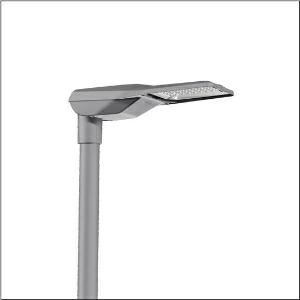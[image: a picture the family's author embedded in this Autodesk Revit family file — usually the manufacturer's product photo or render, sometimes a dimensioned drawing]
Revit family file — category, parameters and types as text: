
# Revit family: streetlight_sl_21_iq_mini___stw1_0a_5xe2e41g08jb_4c9f
name_source: partatom
category: Lighting Fixtures
units: mm (PartAtom-declared; Revit-internal decimal feet)

## family parameters
Cut with Voids When Loaded = No
Host = Face
Light Source = No
Part Type = Normal
Room Calculation Point = No
Round Connector Dimension = Use Diameter
Shared = No

## types (1)
- --- (1 x LED, 11290 lm, 71.6 W, 4000K)
    Apparent Load = 72 VA
    CIE Flux Codes = 39 75 98 100 100
    Color Rendering = 70
    Color Temperature = 4000K
    Default Elevation = 1800 mm
    Description = Streetlight SL 21 iQ mini, mast luminaire, primary light control with lens, of PMMA, primary optical cover: cover, of toughened safety glass, transparent, light distribution: STW1.0a, light emission: direct distribution, primary light characteristic: asymmetric, installation type: post-top, side-entry, LED, High Power LED, rated luminous flux: 11.290lm, luminous efficacy: 158lm/W, light colour: 740, colour temperature: 4000K, control: Street-Remote, Auto-Match, Temp-Guard, Lumen-Switch, Night-Set, Smart-Wire, Light-Fading, Desk-Remote (wireless, voltage-free reading and setting of iQ features in the workshop via application-optimized NFC function/RFID function), optimised constant luminous flux control (CLO 2.0), presetting dimming linear, mains connection: 220..240V, AC, 50/60Hz, start of lifetime: 72W, end of service life: 75W, reduction: 33W, luminaire housing, of diecast aluminium, powder-coated, Siteco® metallic grey (DB 702S), corrosivity category C5 mid according to DIN EN ISO 12944, please order mast flange separately, inclination adjustable: 0°, 5°, 10°, 15°, sealing non-destructively replaceable, multi-level sealing system, length: 628mm, width: 235mm, height: 110mm, mast flange for spigot size: 42mm (side-entry): 5XC10008XM4, 60/48mm (side-entry/post-top): 5XC10108XM2, 76/60mm (side-entry/post-top): 5XC10108XM1, protection rating (complete): IP66, insulation class (complete): insulation class II (safety insulation), certification: CE, ENEC, ENEC+, VDE, impact resistance: IK09, permissible operating ambient temperature for outdoor applications: -40..+50°C, standard-compliant lighting for roads and squares, packaging unit: 1 piece

Light Distribution: STW1.0a
    Height = 110 mm
    Lamp = 1 x LED
    Lamp Light Flux = 11290 lm
    Lamp Power = 71.6 W
    Lamp count = 1
    Length = 625 mm
    Luminous efficacy = 158 lm/W
    Manufacturer = Siteco
    ModVariant = No
    Model = 5XE2E41G08JB
    Number of Poles = 1
    OnlyDefault = Yes
    Power Factor = 1
    Product Name = Streetlight SL 21 iQ mini | STW1.0a
    Product group = mast luminaire | pylon top
    ProductGroupID = 6100
    Protection Class = Protection class II
    Protection Degree = IP 66
    RLX_Detail_Level = 1
    RLX_Emergency_Light_Flux = 0 lm
    RLX_Emergency_Type = 0
    RLX_Emergency_Type_DB = No
    RlxData = <blob elided: 92181 chars, md5=b3a9ba92>
    Socket = socket
    Standby Power = 0 W
    System Light Flux = 11290 lm
    System Power = 72 W
    Type Comments = factory setting: luminous flux: 100 % | dim-lin: 254 | 746 mA
    Type Image = l_1003519.jpg
    URL = http://relux.com
    VarID = @adj_102853
    Voltage = 0 V
    Weight = 0.00 kg
    Width = 234 mm

## geometry (parser evidence)
native form markers: Blend x4, Sweep x12
no freeform markers — native parametric forms only
